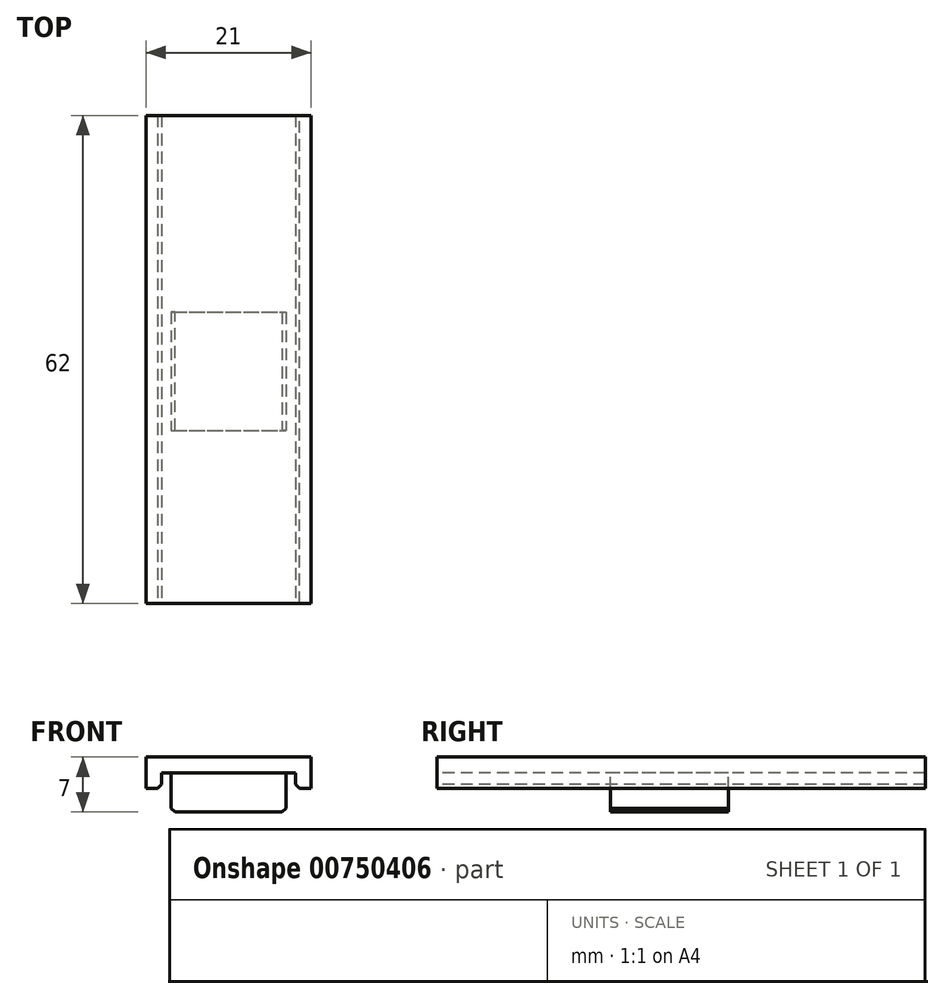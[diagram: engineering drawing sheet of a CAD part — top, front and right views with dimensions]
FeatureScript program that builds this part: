
annotation { "Feature Type Name" : "Feature", "Feature Type Description" : "" }
export const myFeature = defineFeature(function(context is Context, id is Id, definition is map)
    precondition{}
    {
        {
            var Q0;
            Q0=qCreatedBy(makeId("Top.planeOp"),FACE);
            var sketch = newSketch(context, id + "F0", { "sketchPlane" : qUnion([Q0])});
            skLineSegment(sketch, "E0.bottom", {"start": v(0, 0) * mm, "end": v(21, 0) * mm});
            skLineSegment(sketch, "E0.top", {"start": v(0, -62) * mm, "end": v(21, -62) * mm});
            skLineSegment(sketch, "E0.left", {"start": v(0, 0) * mm, "end": v(0, -62) * mm});
            skLineSegment(sketch, "E0.right", {"start": v(21, 0) * mm, "end": v(21, -62) * mm});
            skLineSegment(sketch, "E1.bottom", {"start": v(3.2, -25) * mm, "end": v(17.8, -25) * mm});
            skLineSegment(sketch, "E1.top", {"start": v(3.2, -40) * mm, "end": v(17.8, -40) * mm});
            skLineSegment(sketch, "E1.left", {"start": v(3.2, -25) * mm, "end": v(3.2, -40) * mm});
            skLineSegment(sketch, "E1.right", {"start": v(17.8, -25) * mm, "end": v(17.8, -40) * mm});
            skLineSegment(sketch, "E2.bottom", {"start": v(2, 0) * mm, "end": v(19, 0) * mm});
            skLineSegment(sketch, "E2.top", {"start": v(2, -62) * mm, "end": v(19, -62) * mm});
            skLineSegment(sketch, "E2.left", {"start": v(2, 0) * mm, "end": v(2, -62) * mm});
            skLineSegment(sketch, "E2.right", {"start": v(19, 0) * mm, "end": v(19, -62) * mm});
            skSolve(sketch);
        }
        {
            var Q0;
            {var subQ0=sQuery(id+"F0.wireOp",EDGE,"E0.left");Q0=makeQuery(id+"F0.imprint","IMPRINT",FACE,{"disambiguationData":[TD([[makeQuery(id+"F0.imprint","IMPRINT",EDGE,{"derivedFrom":subQ0}),1.0]])]});}
            var Q1;
            Q1=makeQuery(id+"F0.imprint","IMPRINT",FACE,{"disambiguationData":[TD([[makeQuery(id+"F0.imprint","IMPRINT",EDGE,{"derivedFrom":sQuery(id+"F0.wireOp",EDGE,"E1.bottom")}),1.0]])]});
            var Q2;
            {var subQ0=sQuery(id+"F0.wireOp",EDGE,"E0.right");Q2=makeQuery(id+"F0.imprint","IMPRINT",FACE,{"disambiguationData":[TD([[makeQuery(id+"F0.imprint","IMPRINT",EDGE,{"derivedFrom":subQ0}),-1.0]])]});}
            var Q3;
            Q3=makeQuery(id+"F0.imprint","IMPRINT",FACE,{"disambiguationData":[TD([[makeQuery(id+"F0.imprint","IMPRINT",EDGE,{"derivedFrom":sQuery(id+"F0.wireOp",EDGE,"E1.bottom")}),-1.0]])]});
            extrude(context, id + "F1", {"entities" : qUnion([Q0, Q1, Q2, Q3]), "depth" : 2 * mm, "offsetDistance" : 25 * mm});
        }
        {
            var Q0;
            Q0=makeQuery(id+"F0.imprint","IMPRINT",FACE,{"disambiguationData":[TD([[makeQuery(id+"F0.imprint","IMPRINT",EDGE,{"derivedFrom":sQuery(id+"F0.wireOp",EDGE,"E1.bottom")}),-1.0]])]});
            extrude(context, id + "F2", {"entities" : qUnion([Q0]), "operationType" : NewBodyOperationType.ADD, "oppositeDirection" : true, "depth" : 5 * mm, "offsetDistance" : 25 * mm});
        }
        {
            var Q0;
            {var subQ0=sQuery(id+"F0.wireOp",EDGE,"E0.left");Q0=makeQuery(id+"F0.imprint","IMPRINT",FACE,{"disambiguationData":[TD([[makeQuery(id+"F0.imprint","IMPRINT",EDGE,{"derivedFrom":subQ0}),1.0]])]});}
            var Q1;
            {var subQ0=sQuery(id+"F0.wireOp",EDGE,"E0.right");Q1=makeQuery(id+"F0.imprint","IMPRINT",FACE,{"disambiguationData":[TD([[makeQuery(id+"F0.imprint","IMPRINT",EDGE,{"derivedFrom":subQ0}),-1.0]])]});}
            extrude(context, id + "F3", {"entities" : qUnion([Q0, Q1]), "operationType" : NewBodyOperationType.ADD, "oppositeDirection" : true, "depth" : 2 * mm, "offsetDistance" : 25 * mm});
        }
        {
            var Q0;
            Q0=makeQuery(id+"F3.opExtrude","CAP_EDGE",EDGE,{"disambiguationData":[OSD([sQuery(id+"F0.wireOp",EDGE,"E2.left")])],"isStart":false});
            var Q1;
            Q1=makeQuery(id+"F3.opExtrude","CAP_EDGE",EDGE,{"disambiguationData":[OSD([sQuery(id+"F0.wireOp",EDGE,"E2.right")])],"isStart":false});
            var Q2;
            Q2=makeQuery(id+"F2.opExtrude","CAP_EDGE",EDGE,{"disambiguationData":[OSD([sQuery(id+"F0.wireOp",EDGE,"E1.left")])],"isStart":false});
            var Q3;
            Q3=makeQuery(id+"F2.opExtrude","CAP_EDGE",EDGE,{"disambiguationData":[OSD([sQuery(id+"F0.wireOp",EDGE,"E1.right")])],"isStart":false});
            chamfer(context, id + "F4", {"entities" : qUnion([Q0, Q1, Q2, Q3]), "width" : .5 * mm});
        }
    });
